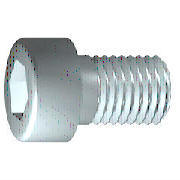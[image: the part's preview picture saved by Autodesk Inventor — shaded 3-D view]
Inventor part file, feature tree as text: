
AUTODESK INVENTOR PART (.ipt)
format: ipt  version: 2022.1 (Build 261234000, 234)  size: 199,168 bytes
history: native  units: mm (DEFAULTED — no unit token found)
features: sketch x2, other x1, extrude x1, plane x1, fillet x1
ambient origin geometry x7: Origin, YZ Plane, XY Plane, X Axis, Y Axis, Z Axis, Center Point
bodies: Solid1 (feature_tree)
feature tree (6):
  other  "Cuerpo"
  extrude  "Ranura"  Depth=3.0mm
  plane  "Work Plane1"
  fillet  "Fillet2"  Radius=3.0mm
  sketch  "Boceto1"  dims[d1=3.75mm d2=0.306825mm d3=3.0mm]
  sketch  "Boceto2"  dims[d4=1.3mm d5=60.0deg d6=3.0mm d7=3.0mm d8=2.886751mm d9=5.5mm d10=90.0deg d11=10.0mm d12=0.0mm d13=3.75mm d14=0.0mm d15=0.306725mm d16=0.306725mm d17=0.3mm d19=0.0mm d26=5.0mm d27=45.0deg d28=0.0mm d29=0.0mm d30=0.1mm]
